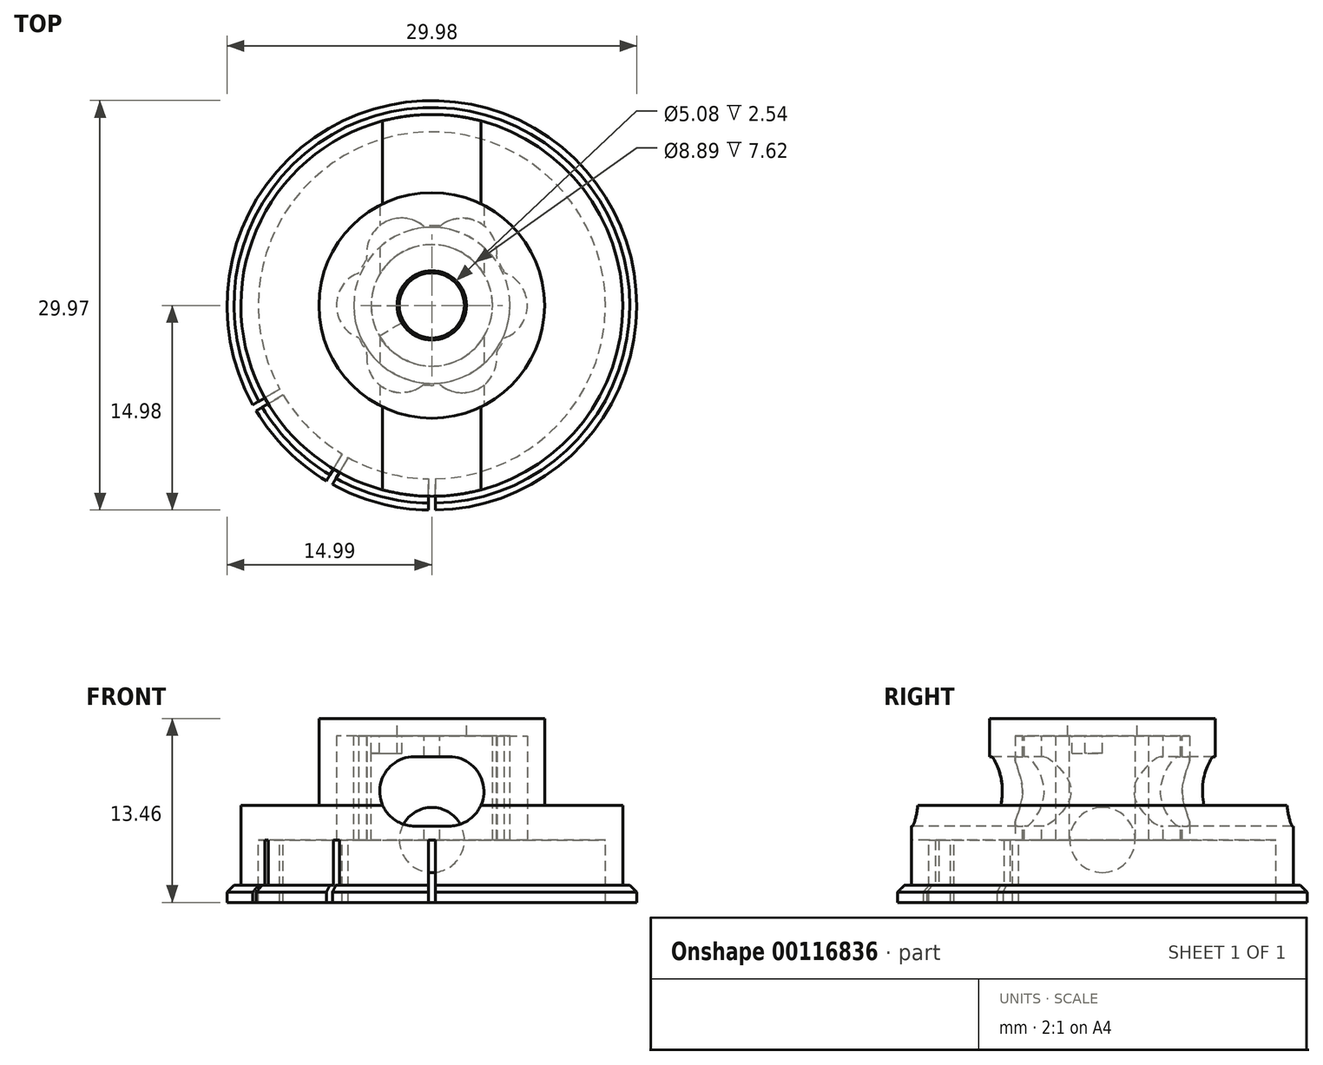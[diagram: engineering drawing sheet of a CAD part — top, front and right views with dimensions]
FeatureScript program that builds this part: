
annotation { "Feature Type Name" : "Feature", "Feature Type Description" : "" }
export const myFeature = defineFeature(function(context is Context, id is Id, definition is map)
    precondition{}
    {
        {
            var Q0;
            Q0=qCreatedBy(makeId("Top.planeOp"),FACE);
            var sketch = newSketch(context, id + "F0", { "sketchPlane" : qUnion([Q0])});
            skCircle(sketch, "E0", {"center": v(0, 0) * mm, "radius": 13.97 * mm});
            skSolve(sketch);
        }
        {
            var Q0;
            Q0 = qSketchRegion(id + "F0", true);
            extrude(context, id + "F1", {"entities" : qUnion([Q0]), "depth" : 2.54 * mm});
        }
        {
            var Q0;
            Q0=makeQuery(id+"F1.opExtrude","CAP_FACE",FACE,{"disambiguationData":[OSD([sQuery(id+"F0.wireOp",EDGE,"E0")])],"isStart":true});
            var sketch = newSketch(context, id + "F2", { "sketchPlane" : qUnion([Q0])});
            skCircle(sketch, "E1.0", {"center": v(0, 0) * mm, "radius": 13.97 * mm});
            skCircle(sketch, "E2.0", {"center": v(0, 0) * mm, "radius": 12.7 * mm});
            skSolve(sketch);
        }
        {
            var Q0;
            Q0 = qSketchRegion(id + "F2", true);
            extrude(context, id + "F3", {"entities" : qUnion([Q0]), "operationType" : NewBodyOperationType.ADD, "depth" : 4.57 * mm});
        }
        {
            var Q0;
            Q0=makeQuery(id+"F3.opExtrude","CAP_FACE",FACE,{"disambiguationData":[OSD([sQuery(id+"F2.wireOp",EDGE,"E1.0"),sQuery(id+"F2.wireOp",EDGE,"E2.0")])],"isStart":false});
            var sketch = newSketch(context, id + "F4", { "sketchPlane" : qUnion([Q0])});
            skCircle(sketch, "E3.0", {"center": v(0, 0) * mm, "radius": 12.7 * mm});
            skCircle(sketch, "E4", {"center": v(0, 0) * mm, "radius": 14.99 * mm});
            skSolve(sketch);
        }
        {
            var Q0;
            Q0 = qSketchRegion(id + "F4", true);
            extrude(context, id + "F5", {"entities" : qUnion([Q0]), "operationType" : NewBodyOperationType.ADD, "oppositeDirection" : true, "depth" : 1.27 * mm});
        }
        {
            var Q0;
            Q0=makeQuery(id+"F5.opExtrude","CAP_EDGE",EDGE,{"disambiguationData":[OSD([sQuery(id+"F4.wireOp",EDGE,"E4")])],"isStart":false});
            chamfer(context, id + "F6", {"entities" : qUnion([Q0]), "width" : 0.5 * mm, "tangentPropagation" : true});
        }
        {
            var Q0;
            Q0=makeQuery(id+"F1.opExtrude","CAP_FACE",FACE,{"disambiguationData":[OSD([sQuery(id+"F0.wireOp",EDGE,"E0")])],"isStart":true});
            var sketch = newSketch(context, id + "F7", { "sketchPlane" : qUnion([Q0])});
            skLineSegment(sketch, "E5", {"start": v(0, 0) * mm, "end": v(0, 17.98) * mm, "construction": true});
            skLineSegment(sketch, "E6", {"start": v(0, 0) * mm, "end": v(-20.11, 11.61) * mm, "construction": true});
            skLineSegment(sketch, "E7", {"start": v(0, 0) * mm, "end": v(-9.14, 15.83) * mm, "construction": true});
            skLineSegment(sketch, "E8.bottom", {"start": v(0.25, 6.34) * mm, "end": v(-0.25, 6.34) * mm});
            skLineSegment(sketch, "E8.top", {"start": v(0.25, 19.05) * mm, "end": v(-0.25, 19.05) * mm});
            skLineSegment(sketch, "E8.left", {"start": v(0.25, 6.34) * mm, "end": v(0.25, 19.05) * mm});
            skLineSegment(sketch, "E8.right", {"start": v(-0.25, 6.34) * mm, "end": v(-0.25, 19.05) * mm});
            skPoint(sketch, "E8.middle", {"position": v(0, 12.7) * mm});
            skLineSegment(sketch, "E9.bottom", {"start": v(-5.37, 3.4) * mm, "end": v(-5.62, 2.95) * mm});
            skLineSegment(sketch, "E9.top", {"start": v(-16.37, 9.74) * mm, "end": v(-16.62, 9.3) * mm});
            skLineSegment(sketch, "E9.left", {"start": v(-5.37, 3.4) * mm, "end": v(-16.37, 9.74) * mm});
            skLineSegment(sketch, "E9.right", {"start": v(-5.62, 2.95) * mm, "end": v(-16.62, 9.3) * mm});
            skPoint(sketch, "E9.middle", {"position": v(-11, 6.35) * mm});
            skLineSegment(sketch, "E10.bottom", {"start": v(-9.74, 16.37) * mm, "end": v(-9.3, 16.62) * mm});
            skLineSegment(sketch, "E10.top", {"start": v(-3.4, 5.37) * mm, "end": v(-2.95, 5.62) * mm});
            skLineSegment(sketch, "E10.left", {"start": v(-9.74, 16.37) * mm, "end": v(-3.4, 5.37) * mm});
            skLineSegment(sketch, "E10.right", {"start": v(-9.3, 16.62) * mm, "end": v(-2.95, 5.62) * mm});
            skPoint(sketch, "E10.middle", {"position": v(-6.35, 11) * mm});
            skCircle(sketch, "E11", {"center": v(0, 0) * mm, "radius": 6.35 * mm, "construction": true});
            skCircle(sketch, "E12", {"center": v(0, 0) * mm, "radius": 19.05 * mm, "construction": true});
            skSolve(sketch);
        }
        {
            var Q0;
            Q0=makeQuery(id+"F1.opExtrude","CAP_FACE",FACE,{"disambiguationData":[OSD([sQuery(id+"F0.wireOp",EDGE,"E0")])],"isStart":false});
            var sketch = newSketch(context, id + "F8", { "sketchPlane" : qUnion([Q0])});
            skCircle(sketch, "E13", {"center": v(0, 0) * mm, "radius": 6.99 * mm});
            skSolve(sketch);
        }
        {
            var Q0;
            Q0=makeQuery(id+"F8.imprint","IMPRINT",FACE,{"disambiguationData":[TD([[makeQuery(id+"F8.imprint","IMPRINT",EDGE,{"derivedFrom":sQuery(id+"F8.wireOp",EDGE,"E13")}),1.0]])]});
            extrude(context, id + "F9", {"entities" : qUnion([Q0]), "operationType" : NewBodyOperationType.REMOVE, "endBound" : BoundingType.THROUGH_ALL, "oppositeDirection" : true, "depth" : 25.4 * mm});
        }
        {
            var Q0;
            Q0=makeQuery(id+"F3.opExtrude","CAP_FACE",FACE,{"disambiguationData":[OSD([sQuery(id+"F2.wireOp",EDGE,"E1.0"),sQuery(id+"F2.wireOp",EDGE,"E2.0")])],"isStart":false});
            var sketch = newSketch(context, id + "F10", { "sketchPlane" : qUnion([Q0])});
            skLineSegment(sketch, "E14", {"start": v(0, 0) * mm, "end": v(-15.33, 0) * mm, "construction": true});
            skLineSegment(sketch, "E15", {"start": v(0, 0) * mm, "end": v(-2.52, -14.3) * mm, "construction": true});
            skArc(sketch, "E16.0", {"start": v(-15.33, 0) * mm, "mid": v(-15.26, -0.9) * mm, "end": v(-15.14, -1.78) * mm});
            skArc(sketch, "E17.0", {"start": v(-12.7, 0) * mm, "mid": v(-12.68, -0.74) * mm, "end": v(-12.61, -1.48) * mm});
            skLineSegment(sketch, "E18", {"start": v(-15.33, 0) * mm, "end": v(-12.7, 0) * mm});
            skLineSegment(sketch, "E19", {"start": v(-2.2, -12.5) * mm, "end": v(-2.52, -14.3) * mm});
            skLineSegment(sketch, "E20", {"start": v(-15.14, -1.78) * mm, "end": v(-12.61, -1.48) * mm});
            skLineSegment(sketch, "E21", {"start": v(-4.98, -13.7) * mm, "end": v(-4.34, -11.94) * mm});
            skLineSegment(sketch, "E22", {"start": v(-12.7, 0) * mm, "end": v(-15.14, -1.78) * mm, "construction": true});
            skLineSegment(sketch, "E23", {"start": v(-4.98, -13.7) * mm, "end": v(-2.2, -12.5) * mm, "construction": true});
            skArc(sketch, "E24.trimOffspring", {"start": v(-4.98, -13.7) * mm, "mid": v(-3.76, -14.05) * mm, "end": v(-2.52, -14.3) * mm});
            skArc(sketch, "E25.trimOffspring", {"start": v(-4.34, -11.94) * mm, "mid": v(-3.28, -12.27) * mm, "end": v(-2.2, -12.5) * mm});
            skSolve(sketch);
        }
        {
            var Q0;
            Q0=makeQuery(id+"F1.opExtrude","CAP_FACE",FACE,{"disambiguationData":[OSD([sQuery(id+"F0.wireOp",EDGE,"E0")])],"isStart":true});
            var sketch = newSketch(context, id + "F11", { "sketchPlane" : qUnion([Q0])});
            skCircle(sketch, "E26.0", {"center": v(0, 0) * mm, "radius": 6.99 * mm, "construction": true});
            skCircle(sketch, "E27.0", {"center": v(0, 0) * mm, "radius": 8.26 * mm});
            skLineSegment(sketch, "E28", {"start": v(0, 0) * mm, "end": v(-8.26, 0) * mm, "construction": true});
            skArc(sketch, "E29", {"start": v(-5.5, 2.31) * mm, "mid": v(-6.99, 0) * mm, "end": v(-5.5, -2.31) * mm});
            skLineSegment(sketch, "E30", {"start": v(0, 0) * mm, "end": v(-3.5, 6.05) * mm, "construction": true});
            skCircle(sketch, "E31", {"center": v(-2.22, 3.85) * mm, "radius": 2.54 * mm, "construction": true});
            skArc(sketch, "E32", {"start": v(-5.5, 2.31) * mm, "mid": v(-4.91, 2.84) * mm, "end": v(-4.75, 3.6) * mm});
            skLineSegment(sketch, "E33", {"start": v(0, 0) * mm, "end": v(-6.05, 3.5) * mm, "construction": true});
            skLineSegment(sketch, "E34", {"start": v(-5.5, 2.31) * mm, "end": v(-5.5, -2.31) * mm, "construction": true});
            skArc(sketch, "E35.1.0", {"start": v(-4.75, -3.6) * mm, "mid": v(-3.5, -6.05) * mm, "end": v(-0.74, -5.91) * mm});
            skArc(sketch, "E35.1.1", {"start": v(-4.75, -3.6) * mm, "mid": v(-4.91, -2.84) * mm, "end": v(-5.5, -2.31) * mm});
            skArc(sketch, "E35.2.0", {"start": v(0.74, -5.91) * mm, "mid": v(3.5, -6.05) * mm, "end": v(4.75, -3.6) * mm});
            skArc(sketch, "E35.2.1", {"start": v(0.74, -5.91) * mm, "mid": v(0, -5.67) * mm, "end": v(-0.74, -5.91) * mm});
            skArc(sketch, "E35.3.0", {"start": v(5.5, -2.31) * mm, "mid": v(6.99, 0) * mm, "end": v(5.5, 2.31) * mm});
            skArc(sketch, "E35.3.1", {"start": v(5.5, -2.31) * mm, "mid": v(4.91, -2.84) * mm, "end": v(4.75, -3.6) * mm});
            skArc(sketch, "E35.4.0", {"start": v(4.75, 3.6) * mm, "mid": v(3.5, 6.05) * mm, "end": v(0.74, 5.91) * mm});
            skArc(sketch, "E35.4.1", {"start": v(4.75, 3.6) * mm, "mid": v(4.91, 2.84) * mm, "end": v(5.5, 2.31) * mm});
            skArc(sketch, "E35.5.0", {"start": v(-0.74, 5.91) * mm, "mid": v(-3.5, 6.05) * mm, "end": v(-4.75, 3.6) * mm});
            skArc(sketch, "E35.5.1", {"start": v(-0.74, 5.91) * mm, "mid": v(0, 5.67) * mm, "end": v(0.74, 5.91) * mm});
            skCircle(sketch, "E36", {"center": v(0, 0) * mm, "radius": 4.45 * mm, "construction": true});
            skSolve(sketch);
        }
        {
            var Q0;
            Q0 = qSketchRegion(id + "F11", true);
            extrude(context, id + "F12", {"entities" : qUnion([Q0]), "operationType" : NewBodyOperationType.ADD, "oppositeDirection" : true, "depth" : 8.9 * mm});
        }
        {
            var Q0;
            Q0=makeQuery(id+"F12.opExtrude","CAP_FACE",FACE,{"disambiguationData":[OSD([sQuery(id+"F11.wireOp",EDGE,"E27.0"),sQuery(id+"F11.wireOp",EDGE,"E29"),sQuery(id+"F11.wireOp",EDGE,"E32"),sQuery(id+"F11.wireOp",EDGE,"E35.1.0"),sQuery(id+"F11.wireOp",EDGE,"E35.1.1"),sQuery(id+"F11.wireOp",EDGE,"E35.2.0"),sQuery(id+"F11.wireOp",EDGE,"E35.2.1"),sQuery(id+"F11.wireOp",EDGE,"E35.3.0"),sQuery(id+"F11.wireOp",EDGE,"E35.3.1"),sQuery(id+"F11.wireOp",EDGE,"E35.4.0"),sQuery(id+"F11.wireOp",EDGE,"E35.4.1"),sQuery(id+"F11.wireOp",EDGE,"E35.5.0"),sQuery(id+"F11.wireOp",EDGE,"E35.5.1")])],"isStart":false});
            var sketch = newSketch(context, id + "F13", { "sketchPlane" : qUnion([Q0])});
            skCircle(sketch, "E37", {"center": v(0, 0) * mm, "radius": 5.84 * mm});
            skSolve(sketch);
        }
        {
            var Q0;
            Q0 = qSketchRegion(id + "F13", true);
            extrude(context, id + "F14", {"entities" : qUnion([Q0]), "operationType" : NewBodyOperationType.REMOVE, "endBound" : BoundingType.THROUGH_ALL, "oppositeDirection" : true, "depth" : 25.4 * mm});
        }
        {
            var Q0;
            Q0=makeQuery(id+"F12.opExtrude","CAP_FACE",FACE,{"disambiguationData":[OSD([sQuery(id+"F11.wireOp",EDGE,"E27.0"),sQuery(id+"F11.wireOp",EDGE,"E29"),sQuery(id+"F11.wireOp",EDGE,"E32"),sQuery(id+"F11.wireOp",EDGE,"E35.1.0"),sQuery(id+"F11.wireOp",EDGE,"E35.1.1"),sQuery(id+"F11.wireOp",EDGE,"E35.2.0"),sQuery(id+"F11.wireOp",EDGE,"E35.2.1"),sQuery(id+"F11.wireOp",EDGE,"E35.3.0"),sQuery(id+"F11.wireOp",EDGE,"E35.3.1"),sQuery(id+"F11.wireOp",EDGE,"E35.4.0"),sQuery(id+"F11.wireOp",EDGE,"E35.4.1"),sQuery(id+"F11.wireOp",EDGE,"E35.5.0"),sQuery(id+"F11.wireOp",EDGE,"E35.5.1")])],"isStart":false});
            var sketch = newSketch(context, id + "F15", { "sketchPlane" : qUnion([Q0])});
            skCircle(sketch, "E38", {"center": v(0, 0) * mm, "radius": 7.11 * mm});
            skCircle(sketch, "E39", {"center": v(0, 0) * mm, "radius": 5.84 * mm, "construction": true});
            skCircle(sketch, "E40", {"center": v(0, 0) * mm, "radius": 2.54 * mm});
            skSolve(sketch);
        }
        {
            var Q0;
            Q0=makeQuery(id+"F15.imprint","IMPRINT",FACE,{"disambiguationData":[TD([[makeQuery(id+"F15.imprint","IMPRINT",EDGE,{"derivedFrom":sQuery(id+"F15.wireOp",EDGE,"E40")}),-1.0]])]});
            var Q1;
            Q1=makeQuery(id+"F1.opExtrude","CAP_FACE",FACE,{"disambiguationData":[OSD([sQuery(id+"F0.wireOp",EDGE,"E0")])],"isStart":false});
            extrude(context, id + "F16", {"entities" : qUnion([Q0]), "operationType" : NewBodyOperationType.ADD, "oppositeDirection" : true, "endBoundEntityFace" : qUnion([Q1]), "depth" : 1.27 * mm});
        }
        {
            var Q0;
            Q0=makeQuery(id+"F16.opExtrude","CAP_FACE",FACE,{"disambiguationData":[OSD([sQuery(id+"F11.wireOp",EDGE,"E29"),sQuery(id+"F11.wireOp",EDGE,"E32"),sQuery(id+"F11.wireOp",EDGE,"E35.1.0"),sQuery(id+"F11.wireOp",EDGE,"E35.1.1"),sQuery(id+"F11.wireOp",EDGE,"E35.2.0"),sQuery(id+"F11.wireOp",EDGE,"E35.2.1"),sQuery(id+"F11.wireOp",EDGE,"E35.3.0"),sQuery(id+"F11.wireOp",EDGE,"E35.3.1"),sQuery(id+"F11.wireOp",EDGE,"E35.4.0"),sQuery(id+"F11.wireOp",EDGE,"E35.4.1"),sQuery(id+"F11.wireOp",EDGE,"E35.5.0"),sQuery(id+"F11.wireOp",EDGE,"E35.5.1"),sQuery(id+"F13.wireOp",EDGE,"E37"),sQuery(id+"F15.wireOp",EDGE,"E40")])],"isStart":false});
            var sketch = newSketch(context, id + "F17", { "sketchPlane" : qUnion([Q0])});
            skCircle(sketch, "E41", {"center": v(0, 0) * mm, "radius": 5.72 * mm});
            skCircle(sketch, "E42.0", {"center": v(0, 0) * mm, "radius": 4.45 * mm});
            skSolve(sketch);
        }
        {
            var Q0;
            Q0=makeQuery(id+"F17.imprint","IMPRINT",FACE,{"disambiguationData":[TD([[makeQuery(id+"F17.imprint","IMPRINT",EDGE,{"derivedFrom":sQuery(id+"F17.wireOp",EDGE,"E41")}),1.0]])]});
            var Q1;
            {var subQ0=sQuery(id+"F0.wireOp",EDGE,"E0");Q1=makeQuery(id+"F12.boolean.opBoolean","MERGE",FACE,{"derivedFrom":[makeQuery(id+"F11ovxtxDOVNGBy_1.boolean.opBoolean","MERGE",FACE,{"derivedFrom":[makeQuery(id+"F1.opExtrude","CAP_FACE",FACE,{"disambiguationData":[OSD([subQ0])],"isStart":true}),makeQuery(id+"F11ovxtxDOVNGBy_1.opExtrude","CAP_FACE",FACE,{"disambiguationData":[OSD([subQ0]),ownerDisambiguation([makeQuery(id+"F11ovxtxDOVNGBy_1.opExtrude","SWEPT_BODY",BODY,{"disambiguationData":[OSD([sQuery(id+"F10.wireOp",EDGE,"E16.0"),sQuery(id+"F10.wireOp",EDGE,"E17.0"),sQuery(id+"F10.wireOp",EDGE,"E18"),sQuery(id+"F10.wireOp",EDGE,"E20")])]})])],"isStart":false}),makeQuery(id+"F11ovxtxDOVNGBy_1.opExtrude","CAP_FACE",FACE,{"disambiguationData":[OSD([subQ0]),ownerDisambiguation([makeQuery(id+"F11ovxtxDOVNGBy_1.opExtrude","SWEPT_BODY",BODY,{"disambiguationData":[OSD([sQuery(id+"F10.wireOp",EDGE,"E19"),sQuery(id+"F10.wireOp",EDGE,"E21"),sQuery(id+"F10.wireOp",EDGE,"E24.trimOffspring"),sQuery(id+"F10.wireOp",EDGE,"E25.trimOffspring")])]})])],"isStart":false})]}),makeQuery(id+"F12.opExtrude","CAP_FACE",FACE,{"disambiguationData":[OSD([sQuery(id+"F11.wireOp",EDGE,"E27.0"),sQuery(id+"F11.wireOp",EDGE,"E29"),sQuery(id+"F11.wireOp",EDGE,"E32"),sQuery(id+"F11.wireOp",EDGE,"E35.1.0"),sQuery(id+"F11.wireOp",EDGE,"E35.1.1"),sQuery(id+"F11.wireOp",EDGE,"E35.2.0"),sQuery(id+"F11.wireOp",EDGE,"E35.2.1"),sQuery(id+"F11.wireOp",EDGE,"E35.3.0"),sQuery(id+"F11.wireOp",EDGE,"E35.3.1"),sQuery(id+"F11.wireOp",EDGE,"E35.4.0"),sQuery(id+"F11.wireOp",EDGE,"E35.4.1"),sQuery(id+"F11.wireOp",EDGE,"E35.5.0"),sQuery(id+"F11.wireOp",EDGE,"E35.5.1")])],"isStart":true})]});}
            extrude(context, id + "F18", {"entities" : qUnion([Q0]), "endBoundEntityFace" : qUnion([Q1]), "depth" : 7.62 * mm});
        }
        {
            var Q0;
            Q0=qCreatedBy(makeId("Front.planeOp"),FACE);
            var sketch = newSketch(context, id + "F19", { "sketchPlane" : qUnion([Q0])});
            skLineSegment(sketch, "E43.bottom", {"start": v(1.27, 1.02) * mm, "end": v(-1.27, 1.02) * mm});
            skLineSegment(sketch, "E43.top", {"start": v(1.27, 6.1) * mm, "end": v(-1.27, 6.1) * mm});
            skLineSegment(sketch, "E43.left", {"start": v(1.27, 1.02) * mm, "end": v(1.27, 6.1) * mm, "construction": true});
            skLineSegment(sketch, "E43.right", {"start": v(-1.27, 1.02) * mm, "end": v(-1.27, 6.1) * mm, "construction": true});
            skArc(sketch, "E44", {"start": v(-1.27, 6.1) * mm, "mid": v(-3.81, 3.56) * mm, "end": v(-1.27, 1.02) * mm});
            skArc(sketch, "E45", {"start": v(1.27, 1.02) * mm, "mid": v(3.81, 3.56) * mm, "end": v(1.27, 6.1) * mm});
            skLineSegment(sketch, "E46", {"start": v(0, 7.62) * mm, "end": v(0, 0) * mm, "construction": true});
            skSolve(sketch);
        }
        {
            var Q0;
            Q0 = qSketchRegion(id + "F19", true);
            extrude(context, id + "F20", {"entities" : qUnion([Q0]), "operationType" : NewBodyOperationType.REMOVE, "endBound" : BoundingType.THROUGH_ALL, "oppositeDirection" : true, "depth" : 25.4 * mm, "hasSecondDirection" : true, "secondDirectionBound" : BoundingType.THROUGH_ALL, "secondDirectionOppositeDirection" : false, "secondDirectionDepth" : 25.4 * mm});
        }
        {
            var Q0;
            Q0=qCreatedBy(makeId("Front.planeOp"),FACE);
            var sketch = newSketch(context, id + "F21", { "sketchPlane" : qUnion([Q0])});
            skArc(sketch, "E47", {"start": v(0, -2.38) * mm, "mid": v(2.38, 0) * mm, "end": v(0, 2.38) * mm});
            skLineSegment(sketch, "E48", {"start": v(0, 2.38) * mm, "end": v(0, -2.38) * mm});
            skSolve(sketch);
        }
        {
            var Q0;
            Q0 = qSketchRegion(id + "F21", true);
            var Q1;
            Q1=sQuery(id+"F21.wireOp",EDGE,"E48");
            revolve(context, id + "F22", {"entities" : qUnion([Q0]), "axis" : qUnion([Q1]), "revolveType" : RevolveType.FULL});
        }
        {
            var Q0;
            Q0=makeQuery(id+"F18.opExtrude","CAP_FACE",FACE,{"disambiguationData":[OSD([sQuery(id+"F17.wireOp",EDGE,"E41"),sQuery(id+"F17.wireOp",EDGE,"E42.0")])],"isStart":true});
            var sketch = newSketch(context, id + "F23", { "sketchPlane" : qUnion([Q0])});
            skArc(sketch, "E49.0", {"start": v(-4.45, 0) * mm, "mid": v(-4.3, -1.15) * mm, "end": v(-3.85, -2.22) * mm});
            skLineSegment(sketch, "E50", {"start": v(-4.45, 0) * mm, "end": v(-2.54, 0) * mm});
            skLineSegment(sketch, "E51", {"start": v(-3.85, -2.22) * mm, "end": v(-2.2, -1.27) * mm});
            skArc(sketch, "E52", {"start": v(-2.54, 0) * mm, "mid": v(-2.45, -0.66) * mm, "end": v(-2.2, -1.27) * mm});
            skSolve(sketch);
        }
        {
            var Q0;
            Q0 = qSketchRegion(id + "F23", true);
            extrude(context, id + "F24", {"entities" : qUnion([Q0]), "operationType" : NewBodyOperationType.ADD, "oppositeDirection" : true, "depth" : 1.27 * mm});
        }
        {
            var Q0;
            Q0 = qSketchRegion(id + "F7", true);
            extrude(context, id + "F25", {"entities" : qUnion([Q0]), "operationType" : NewBodyOperationType.REMOVE, "endBound" : BoundingType.THROUGH_ALL, "depth" : 25.4 * mm});
        }
    });
